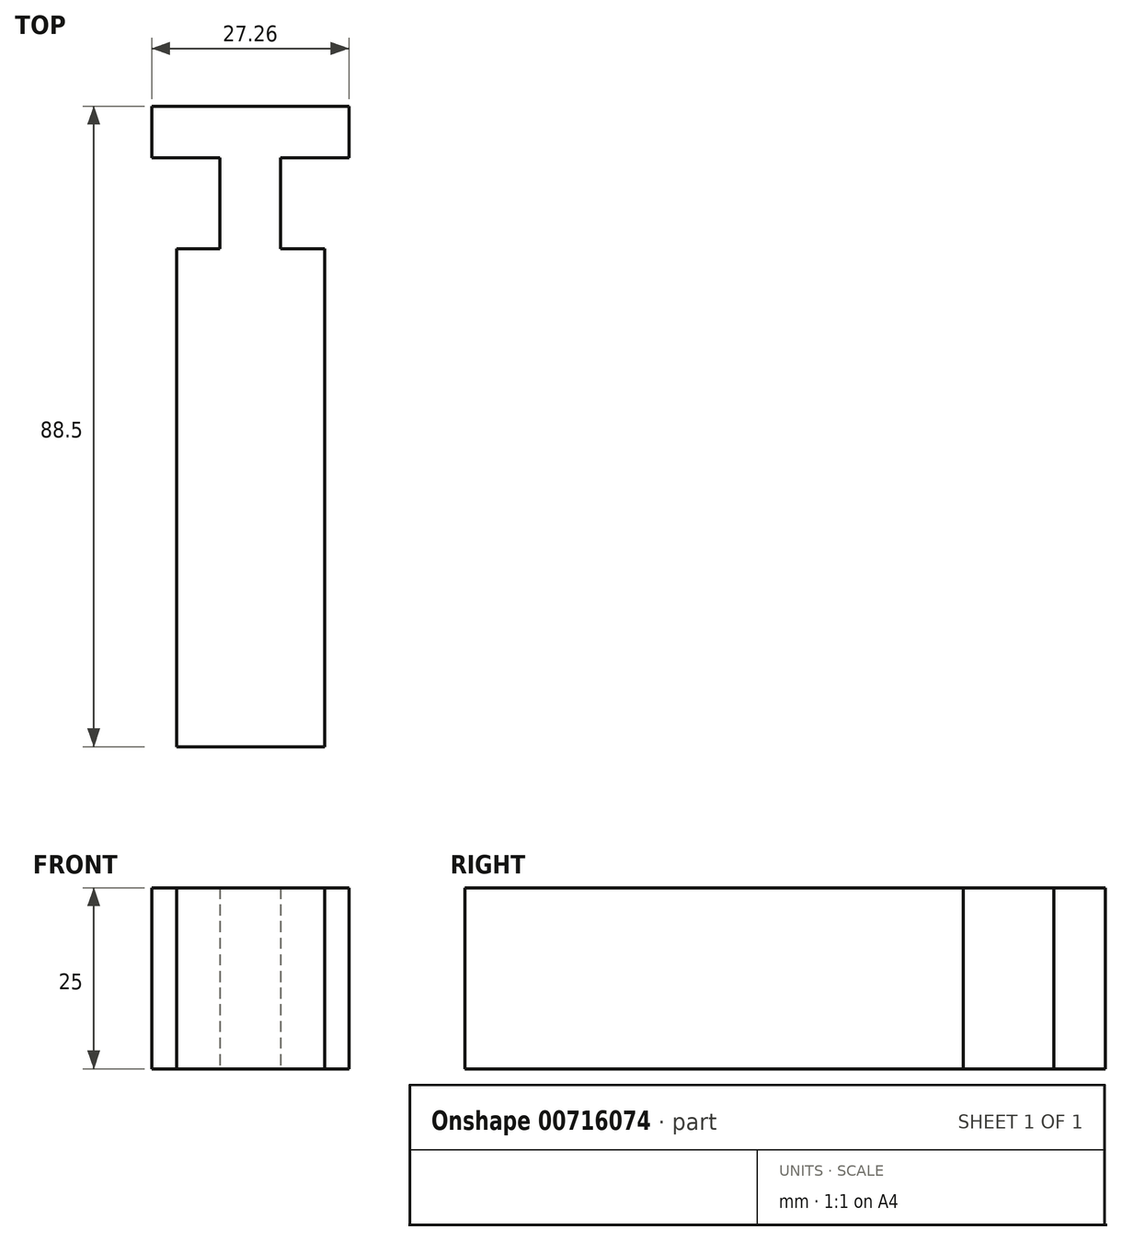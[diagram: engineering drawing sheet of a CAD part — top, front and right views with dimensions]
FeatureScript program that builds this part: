
annotation { "Feature Type Name" : "Feature", "Feature Type Description" : "" }
export const myFeature = defineFeature(function(context is Context, id is Id, definition is map)
    precondition{}
    {
        {
            var Q0;
            Q0=qCreatedBy(makeId("Top.planeOp"),FACE);
            var sketch = newSketch(context, id + "F0", { "sketchPlane" : qUnion([Q0])});
            skLineSegment(sketch, "E0.bottom", {"start": v(13.57, 18.82) * mm, "end": v(-13.7, 18.82) * mm});
            skLineSegment(sketch, "E0.top", {"start": v(13.57, 11.7) * mm, "end": v(4.13, 11.7) * mm});
            skLineSegment(sketch, "E0.left", {"start": v(13.57, 18.82) * mm, "end": v(13.57, 11.7) * mm});
            skLineSegment(sketch, "E0.right", {"start": v(-13.7, 18.82) * mm, "end": v(-13.7, 11.7) * mm});
            skPoint(sketch, "E0.middle", {"position": v(-0.06, 15.25) * mm});
            skLineSegment(sketch, "E1.left", {"start": v(4.13, -0.85) * mm, "end": v(4.13, 11.7) * mm});
            skLineSegment(sketch, "E1.right", {"start": v(-4.25, -0.85) * mm, "end": v(-4.25, 11.7) * mm});
            skPoint(sketch, "E1.middle", {"position": v(-0.06, 0.02) * mm});
            skPoint(sketch, "E2.orphan", {"position": v(4.13, 14.72) * mm});
            skPoint(sketch, "E3.orphan", {"position": v(-4.25, 14.72) * mm});
            skLineSegment(sketch, "E4.trimOffspring", {"start": v(-4.25, 11.7) * mm, "end": v(-13.7, 11.7) * mm});
            skLineSegment(sketch, "E5.bottom", {"start": v(10.23, -69.68) * mm, "end": v(-10.23, -69.68) * mm});
            skLineSegment(sketch, "E5.top", {"start": v(10.23, -0.85) * mm, "end": v(-10.23, -0.85) * mm});
            skLineSegment(sketch, "E5.left", {"start": v(10.23, -69.68) * mm, "end": v(10.23, -0.85) * mm});
            skLineSegment(sketch, "E5.right", {"start": v(-10.23, -69.68) * mm, "end": v(-10.23, -0.85) * mm});
            skPoint(sketch, "E5.middle", {"position": v(0, -35.27) * mm});
            skPoint(sketch, "E6.orphan", {"position": v(-4.25, -14.68) * mm});
            skPoint(sketch, "E7.orphan", {"position": v(4.13, -14.68) * mm});
            skSolve(sketch);
        }
        {
            var Q0;
            Q0=makeQuery(id+"F0.imprint","IMPRINT",FACE,{"disambiguationData":[TD([[makeQuery(id+"F0.imprint","IMPRINT",EDGE,{"derivedFrom":sQuery(id+"F0.wireOp",EDGE,"E5.bottom")}),-1.0]])]});
            var Q1;
            Q1 = qSketchRegion(id + "F0", true);
            extrude(context, id + "F1", {"entities" : qUnion([Q0, Q1]), "depth" : 25 * mm, "offsetDistance" : 25 * mm});
        }
    });
